# Revit family: NaughtOne_HatchSingleSeatWork
name_source: partatom
category: Furniture
units: mm (PartAtom-declared; Revit-internal decimal feet)

## family parameters
Always vertical = Yes
Cut with Voids When Loaded = No
Enable Cutting in Views = No
Render Appearance Source = Family Geometry
Room Calculation Point = No
Shared = Yes
Work Plane-Based = No

## types (6) — shared parameters
Assembly Code = E2020200
AssetType = Moveable
BIMObjectName = Naughtone_Seating_Hatch
Category = Pr_40_50_12: Chairs, seats and benches
CodePerformance = PASSED BSEN 16139
Color = Various
DurationUnit = year
Export Type to IFC As = IfcFurnishingElementType
Finish = Upholstered
HasOneArmL = No
IfcExportAs = IfcFurnishingElementType
IfcExportType = SOFA
Is2Seat = No
Is3Seat = No
IsChair = No
LeftOffset = 10.04 "
MainColor = Various
ManufacturerAddressUK = naughtone, Knaresborough Tech Park, Manse Lane, Knaresborough, HG5 8LF
ManufacturerName = Naughtone
ManufacturerURL = www.naughtone.com
Material = Fabric, leather/steel/solid wood/beech ply/foam
ModelNumber = HAT1NA
ModelReference = Hatch Chair No Arms
NBSDescription = Seating
NBSReference = 45-35-72/352
Name = Seating_Hatch_Naughtone
NominalHeight = 26.97 "
NominalWidth = 27.17 "
Package Qty = 1
Product Documentation Link = http://www.naughtone.com
ProductInformation = www.naughtone.com/portfolio-view/hatch
RightOffset = 10.04 "
Shape = Rectangular
Size = 510x690x685mm
SustainabilityPerformance = FSC certified. FISP certified. ISO 14001 certified
Type IFC Predefined Type = SOFA
Uniclass2015Description = Chairs, seats and benches
Uniclass2015Reference = Pr_40_50_12
Uniclass2015Version = Products v1.5
Version = 1
VoidOffset2Seat = 0.39 "
VoidOffset3Seat = 0.39 "
VoidOffsetCentre = 10.04 "
WarrantyDurationLabor = 5
WarrantyDurationParts = 5
WarrantyDurationUnit = year
zero-valued in all types: Default Elevation

## per-type parameters (varying)
| type | Description | HasNoArms | HasOneArmR | HasTwoArms | Model |
| No Arms Single Fabric Work Ht | Hatch Single Seat No Arms Work height 18 inch seat height Single Fabric | Yes | No | No | NOHAN120W1 |
| No Arms Multiple Fabric Work Ht | Hatch Single Seat No Arms Multiple Work height 18 inch seat height Multiple Fabric | Yes | No | No | NOHAN120W2 |
| One Arm Corner Single Fabric Work Ht | Hatch Single Seat One Arm Corner Single Work height 18 inch seat height Single Fabric | No | Yes | No | NOHAN130W1 |
| One Arm Corner Multiple Fabric Work Ht | Hatch Single Seat One Arm Corner Multiple Work height 18 inch seat height Multiple Fabric | No | Yes | No | NOHAN130W2 |
| Two Arms Single Fabric Work Ht | Hatch Single Seat Two Arms Single Work height 18 inch seat height Single Fabric | No | No | Yes | NOHAN140W1 |
| Two Arms Multiple Fabric Work Ht | Hatch Single Seat Two Arms Multiple Work height 18 inch seat height Multiple Fabric | No | No | Yes | NOHAN140W2 |

## geometry (parser evidence)
native form markers: Sweep x4
no freeform markers — native parametric forms only
